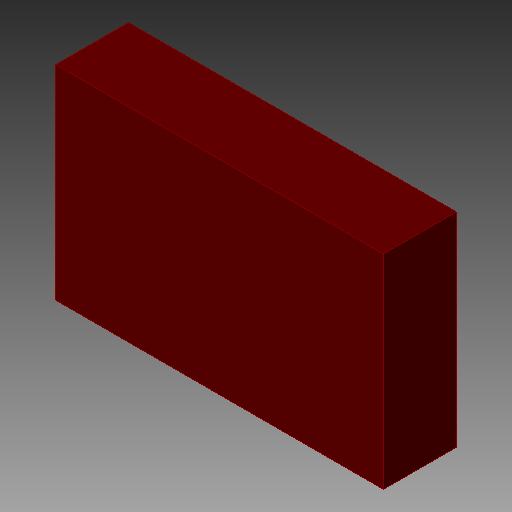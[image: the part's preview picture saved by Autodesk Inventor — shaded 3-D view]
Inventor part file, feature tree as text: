
AUTODESK INVENTOR PART (.ipt)
format: ipt  version: 2018 (Build 220112000, 112)  size: 80,896 bytes
history: native  units: in
note: dims shown in document units (in); Inventor stores cm internally (conversion verified against a paired STEP export)
features: other x1, extrude x1
ambient origin geometry x8: Origin, YZ Plane, XZ Plane, XY Plane, X Axis, Y Axis, Z Axis, Center Point
bodies: Solid1 (feature_tree)
feature tree (2):
  other  "MURATA-FILTER_CSTCR, PIEZO_CSTCR4M00G15L99_95"
  extrude  "Extrusion1"  Depth=0.0394in TaperAngle=0.0deg
